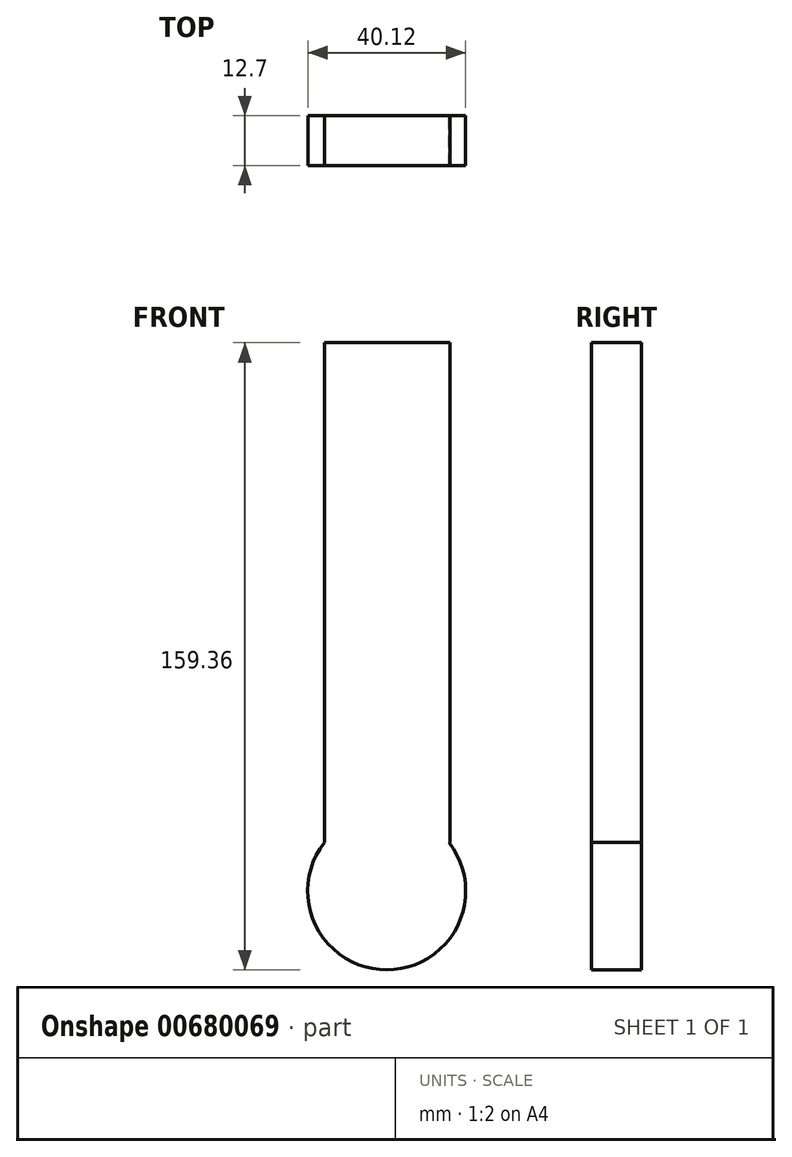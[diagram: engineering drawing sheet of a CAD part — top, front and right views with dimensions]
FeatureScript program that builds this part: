
annotation { "Feature Type Name" : "Feature", "Feature Type Description" : "" }
export const myFeature = defineFeature(function(context is Context, id is Id, definition is map)
    precondition{}
    {
        {
            var Q0;
            Q0=qCreatedBy(makeId("Front.planeOp"),FACE);
            var sketch = newSketch(context, id + "F0", { "sketchPlane" : qUnion([Q0])});
            skCircle(sketch, "E0", {"center": v(0, 0) * mm, "radius": 20.06 * mm});
            skLineSegment(sketch, "E1.bottom", {"start": v(-15.85, 12.3) * mm, "end": v(16.05, 12.3) * mm});
            skLineSegment(sketch, "E1.top", {"start": v(-15.85, 139.3) * mm, "end": v(16.05, 139.3) * mm});
            skLineSegment(sketch, "E1.left", {"start": v(-15.85, 12.3) * mm, "end": v(-15.85, 139.3) * mm});
            skLineSegment(sketch, "E1.right", {"start": v(16.05, 12.3) * mm, "end": v(16.05, 139.3) * mm});
            skSolve(sketch);
        }
        {
            var Q0;
            {var subQ0=sQuery(id+"F0.wireOp",EDGE,"E1.bottom");var subQ1=sQuery(id+"F0.wireOp",EDGE,"E0");var subQ3=makeQuery(id+"F0.imprint","INTERSECT",VERTEX,{"derivedFrom":[subQ1,subQ0]});Q0=makeQuery(id+"F0.imprint","IMPRINT",FACE,{"disambiguationData":[TD([[makeQuery(id+"F0.imprint","IMPRINT",EDGE,{"disambiguationData":[TD([[subQ3,1.0]])],"derivedFrom":subQ1}),1.0]])]});}
            var Q1;
            Q1=makeQuery(id+"F0.imprint","IMPRINT",FACE,{"disambiguationData":[TD([[makeQuery(id+"F0.imprint","IMPRINT",EDGE,{"derivedFrom":sQuery(id+"F0.wireOp",EDGE,"E1.top")}),-1.0]])]});
            var Q2;
            {var subQ0=sQuery(id+"F0.wireOp",EDGE,"E1.bottom");var subQ1=sQuery(id+"F0.wireOp",EDGE,"E0");var subQ3=makeQuery(id+"F0.imprint","INTERSECT",VERTEX,{"derivedFrom":[subQ1,subQ0]});Q2=makeQuery(id+"F0.imprint","IMPRINT",FACE,{"disambiguationData":[TD([[makeQuery(id+"F0.imprint","IMPRINT",EDGE,{"disambiguationData":[TD([[subQ3,-1.0]])],"derivedFrom":subQ1}),1.0]])]});}
            extrude(context, id + "F1", {"entities" : qUnion([Q0, Q1, Q2]), "depth" : 12.7 * mm, "offsetDistance" : 25.4 * mm});
        }
    });
